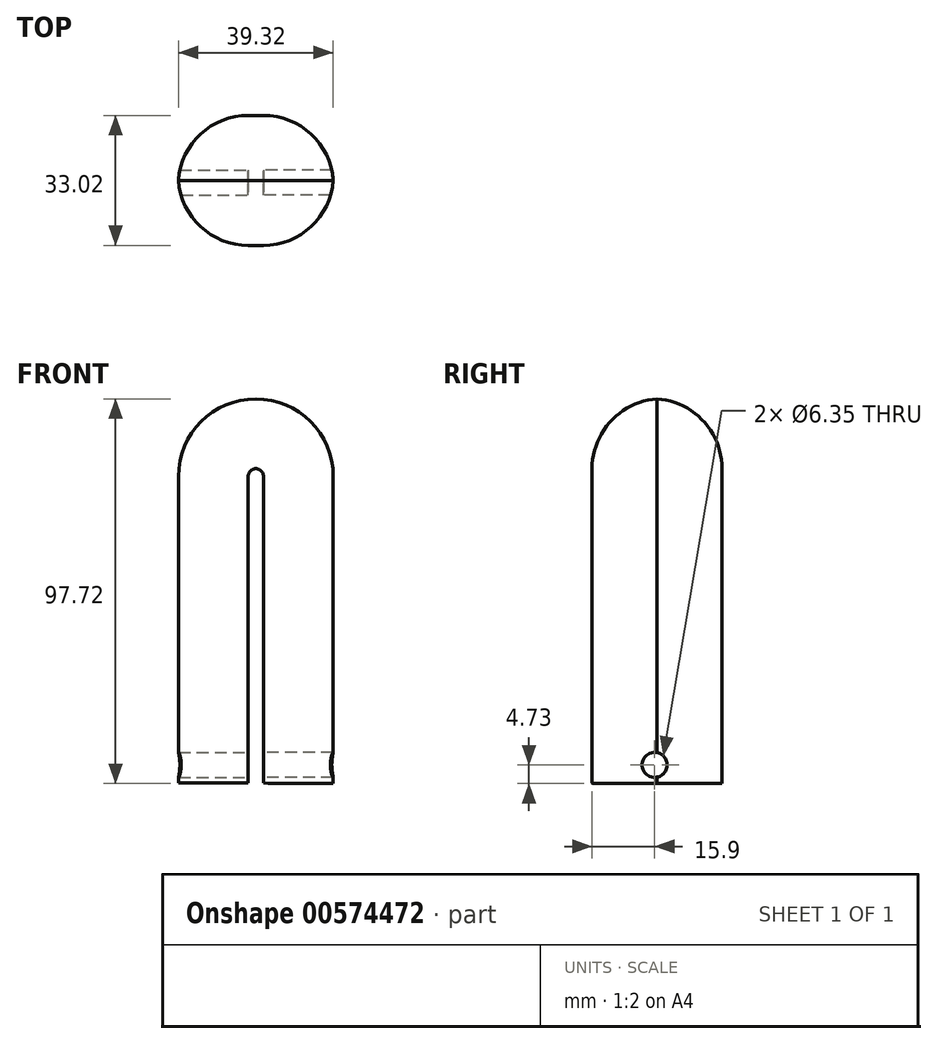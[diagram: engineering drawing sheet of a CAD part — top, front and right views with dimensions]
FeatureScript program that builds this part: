
annotation { "Feature Type Name" : "Feature", "Feature Type Description" : "" }
export const myFeature = defineFeature(function(context is Context, id is Id, definition is map)
    precondition{}
    {
        {
            var Q0;
            Q0=qCreatedBy(makeId("Front.planeOp"),FACE);
            var sketch = newSketch(context, id + "F0", { "sketchPlane" : qUnion([Q0])});
            skArc(sketch, "E0", {"start": v(19.7, 0) * mm, "mid": v(0, 19.7) * mm, "end": v(-19.7, 0) * mm});
            skLineSegment(sketch, "E1", {"start": v(-19.7, 0) * mm, "end": v(-19.7, -77.85) * mm});
            skLineSegment(sketch, "E2", {"start": v(19.7, 0) * mm, "end": v(19.7, -78.06) * mm});
            skLineSegment(sketch, "E3", {"start": v(19.7, -78.06) * mm, "end": v(-19.7, -77.85) * mm});
            skLineSegment(sketch, "E4", {"start": v(-19.7, 0) * mm, "end": v(19.7, 0) * mm});
            skSolve(sketch);
        }
        {
            var Q0;
            Q0 = qSketchRegion(id + "F0", true);
            extrude(context, id + "F1", {"entities" : qUnion([Q0]), "depth" : 33.02 * mm, "offsetDistance" : 25.4 * mm});
        }
        {
            var Q0;
            Q0=makeQuery(id+"F1.opExtrude","CAP_EDGE",EDGE,{"disambiguationData":[OSD([sQuery(id+"F0.wireOp",EDGE,"E2")])],"isStart":true});
            var Q1;
            Q1=makeQuery(id+"F1.opExtrude","CAP_EDGE",EDGE,{"disambiguationData":[OSD([sQuery(id+"F0.wireOp",EDGE,"E2")])],"isStart":false});
            fillet(context, id + "F2", {"entities" : qUnion([Q0, Q1]), "radius" : 17.78 * mm, "tangentPropagation" : true, "allowEdgeOverflow" : false});
        }
        {
            var Q0;
            Q0=makeQuery(id+"F1.opExtrude","CAP_FACE",FACE,{"disambiguationData":[OSD([sQuery(id+"F0.wireOp",EDGE,"E0"),sQuery(id+"F0.wireOp",EDGE,"E1"),sQuery(id+"F0.wireOp",EDGE,"E2"),sQuery(id+"F0.wireOp",EDGE,"E3")])],"isStart":false});
            extrude(context, id + "F3", {"entities" : qUnion([Q0]), "operationType" : NewBodyOperationType.REMOVE, "oppositeDirection" : true, "depth" : 127 * mm, "offsetDistance" : 25.4 * mm});
        }
        {
            var Q0;
            Q0=qCreatedBy(makeId("Right.planeOp"),FACE);
            var sketch = newSketch(context, id + "F4", { "sketchPlane" : qUnion([Q0])});
            skPoint(sketch, "E5", {"position": v(-17.12, -73.33) * mm});
            skSolve(sketch);
        }
        {
            var Q0;
            Q0=sQuery(id+"F4.wireOp",VERTEX,"E5");
            var Q1;
            Q1=makeQuery(id+"F1.opExtrude","SWEPT_BODY",BODY,{"disambiguationData":[OSD([sQuery(id+"F0.wireOp",EDGE,"E0"),sQuery(id+"F0.wireOp",EDGE,"E1"),sQuery(id+"F0.wireOp",EDGE,"E2"),sQuery(id+"F0.wireOp",EDGE,"E3")])]});
            hole(context, id + "F5", {"style" : HoleStyle.SIMPLE, "endStyle" : HoleEndStyle.THROUGH, "holeDiameter" : 6.35 * mm, "isTappedThrough" : true, "tappedDepth" : 12.7 * mm, "tapClearance" : 3, "locations" : qUnion([Q0]), "scope" : qUnion([Q1])});
        }
        {
            var Q0;
            Q0=sQuery(id+"F4.wireOp",VERTEX,"E5");
            var Q1;
            Q1=makeQuery(id+"F1.opExtrude","SWEPT_BODY",BODY,{"disambiguationData":[OSD([sQuery(id+"F0.wireOp",EDGE,"E0"),sQuery(id+"F0.wireOp",EDGE,"E1"),sQuery(id+"F0.wireOp",EDGE,"E2"),sQuery(id+"F0.wireOp",EDGE,"E3")])]});
            hole(context, id + "F6", {"style" : HoleStyle.SIMPLE, "endStyle" : HoleEndStyle.THROUGH, "oppositeDirection" : true, "holeDiameter" : 6.35 * mm, "isTappedThrough" : true, "tappedDepth" : 12.7 * mm, "tapClearance" : 3, "locations" : qUnion([Q0]), "scope" : qUnion([Q1])});
        }
    });
